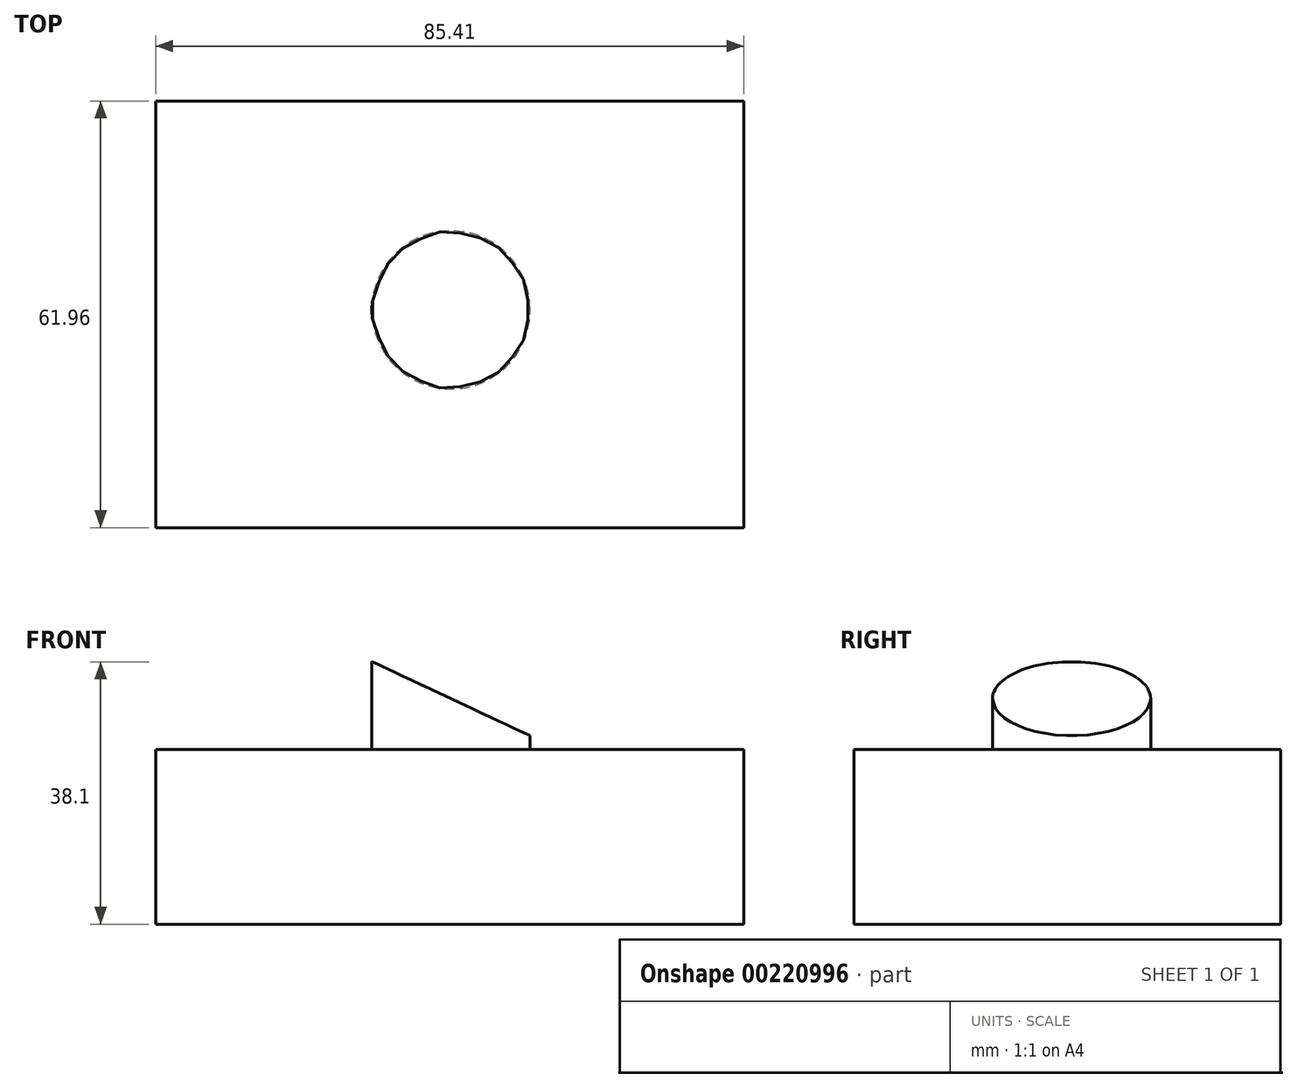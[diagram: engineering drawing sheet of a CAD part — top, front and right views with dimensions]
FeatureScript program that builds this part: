
annotation { "Feature Type Name" : "Feature", "Feature Type Description" : "" }
export const myFeature = defineFeature(function(context is Context, id is Id, definition is map)
    precondition{}
    {
        {
            var Q0;
            Q0=qCreatedBy(makeId("Top.planeOp"),FACE);
            var sketch = newSketch(context, id + "F0", { "sketchPlane" : qUnion([Q0])});
            skLineSegment(sketch, "E0.bottom", {"start": v(-36.84, 30.34) * mm, "end": v(48.57, 30.34) * mm});
            skLineSegment(sketch, "E0.top", {"start": v(-36.84, -31.62) * mm, "end": v(48.57, -31.62) * mm});
            skLineSegment(sketch, "E0.left", {"start": v(-36.84, 30.34) * mm, "end": v(-36.84, -31.62) * mm});
            skLineSegment(sketch, "E0.right", {"start": v(48.57, 30.34) * mm, "end": v(48.57, -31.62) * mm});
            skSolve(sketch);
        }
        {
            var Q0;
            Q0=makeQuery(id+"F0.imprint","IMPRINT",FACE,{"disambiguationData":[TD([[makeQuery(id+"F0.imprint","IMPRINT",EDGE,{"derivedFrom":sQuery(id+"F0.wireOp",EDGE,"E0.bottom")}),-1.0]])]});
            extrude(context, id + "F1", {"entities" : qUnion([Q0]), "depth" : 25.4 * mm});
        }
        {
            var Q0;
            Q0=makeQuery(id+"F1.opExtrude","CAP_FACE",FACE,{"disambiguationData":[OSD([sQuery(id+"F0.wireOp",EDGE,"E0.bottom"),sQuery(id+"F0.wireOp",EDGE,"E0.top"),sQuery(id+"F0.wireOp",EDGE,"E0.left"),sQuery(id+"F0.wireOp",EDGE,"E0.right")])],"isStart":false});
            var sketch = newSketch(context, id + "F2", { "sketchPlane" : qUnion([Q0])});
            skCircle(sketch, "E1", {"center": v(6.05, 0) * mm, "radius": 11.5 * mm});
            skSolve(sketch);
        }
        {
            var Q0;
            Q0=makeQuery(id+"F2.imprint","IMPRINT",FACE,{"disambiguationData":[TD([[makeQuery(id+"F2.imprint","IMPRINT",EDGE,{"derivedFrom":sQuery(id+"F2.wireOp",EDGE,"E1")}),1.0]])]});
            extrude(context, id + "F3", {"entities" : qUnion([Q0]), "operationType" : NewBodyOperationType.ADD, "depth" : 12.7 * mm});
        }
        {
            var Q0;
            Q0=qCreatedBy(makeId("Front.planeOp"),FACE);
            var sketch = newSketch(context, id + "F4", { "sketchPlane" : qUnion([Q0])});
            skLineSegment(sketch, "E2", {"start": v(-6.26, 38.52) * mm, "end": v(18.03, 27.14) * mm});
            skLineSegment(sketch, "E3", {"start": v(18.03, 27.14) * mm, "end": v(18.03, 39) * mm});
            skLineSegment(sketch, "E4", {"start": v(18.03, 39) * mm, "end": v(-6.26, 38.52) * mm});
            skSolve(sketch);
        }
        {
            var Q0;
            Q0 = qSketchRegion(id + "F4", true);
            extrude(context, id + "F5", {"entities" : qUnion([Q0]), "operationType" : NewBodyOperationType.REMOVE, "endBound" : BoundingType.SYMMETRIC, "oppositeDirection" : true, "depth" : 50.8 * mm});
        }
    });
